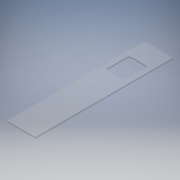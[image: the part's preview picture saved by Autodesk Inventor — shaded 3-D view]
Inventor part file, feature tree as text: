
AUTODESK INVENTOR PART (.ipt)
format: ipt  version: 2018 (Build 220112000, 112)  size: 129,536 bytes
history: native  units: mm
features: extrude x2, fillet x1, reference x1
ambient origin geometry x8: Origin, YZ Plane, XZ Plane, XY Plane, X Axis, Y Axis, Z Axis, Center Point
bodies: Volumenkörper1 (feature_tree)
feature tree (4):
  extrude  "Extrusion1"  Depth=583.0mm
  extrude  "Extrusion2"  Depth=121.0mm
  fillet  "Rundung1"  Radius=6.0mm
  reference  "Referenz1"
